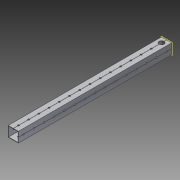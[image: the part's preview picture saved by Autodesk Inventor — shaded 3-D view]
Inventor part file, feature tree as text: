
AUTODESK INVENTOR PART (.ipt)
format: ipt  version: 2014 SP1 (Build 180222100, 222)  size: 1,264,640 bytes
history: native  units: in
note: dims shown in document units (in); Inventor stores cm internally (conversion verified against a paired STEP export)
features: extrude x2, sketch x2, pattern_circular x1, other x1, plane x1, imported_body x1
ambient origin geometry x8: Origin, YZ Plane, XZ Plane, XY Plane, X Axis, Y Axis, Z Axis, Center Point
bodies: Body1 (feature_tree)
feature tree (8):
  pattern_circular  "CirPattern2"
  other  "217-3426-STEP1"
  plane  "Work Plane1"
  extrude  "Extrusion1"  Depth=3937.0079in TaperAngle=0.0deg
  extrude  "Extrusion2"  Depth=0.5in
  imported_body  "Base1"
  sketch  "Sketch1"  dims[d0=-15.0in d1=3937.0079in d2=0.0in]
  sketch  "Sketch3"  dims[d4=3.937in d5=0.0in d6=0.5in d7=0.5in d8=0.5in]
